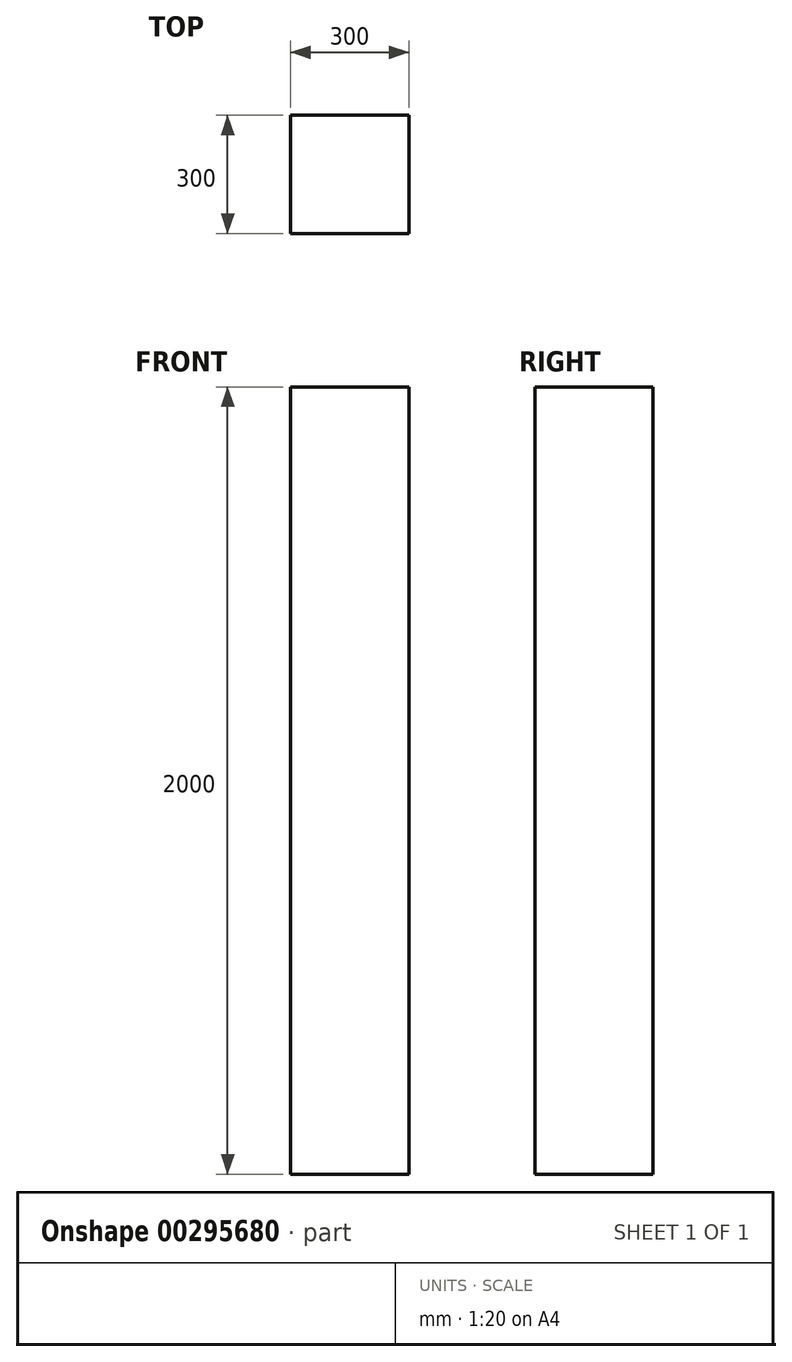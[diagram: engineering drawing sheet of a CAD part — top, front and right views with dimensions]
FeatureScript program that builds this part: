
annotation { "Feature Type Name" : "Feature", "Feature Type Description" : "" }
export const myFeature = defineFeature(function(context is Context, id is Id, definition is map)
    precondition{}
    {
        {
            var Q0;
            Q0=qCreatedBy(makeId("Top.planeOp"),FACE);
            var sketch = newSketch(context, id + "F0", { "sketchPlane" : qUnion([Q0])});
            skLineSegment(sketch, "E0.bottom", {"start": v(-150, -150) * mm, "end": v(150, -150) * mm});
            skLineSegment(sketch, "E0.top", {"start": v(-150, 150) * mm, "end": v(150, 150) * mm});
            skLineSegment(sketch, "E0.left", {"start": v(-150, -150) * mm, "end": v(-150, 150) * mm});
            skLineSegment(sketch, "E0.right", {"start": v(150, -150) * mm, "end": v(150, 150) * mm});
            skPoint(sketch, "E0.middle", {"position": v(0, 0) * mm});
            skSolve(sketch);
        }
        {
            var Q0;
            Q0 = qSketchRegion(id + "F0", true);
            extrude(context, id + "F1", {"entities" : qUnion([Q0]), "depth" : 2000 * mm});
        }
    });
